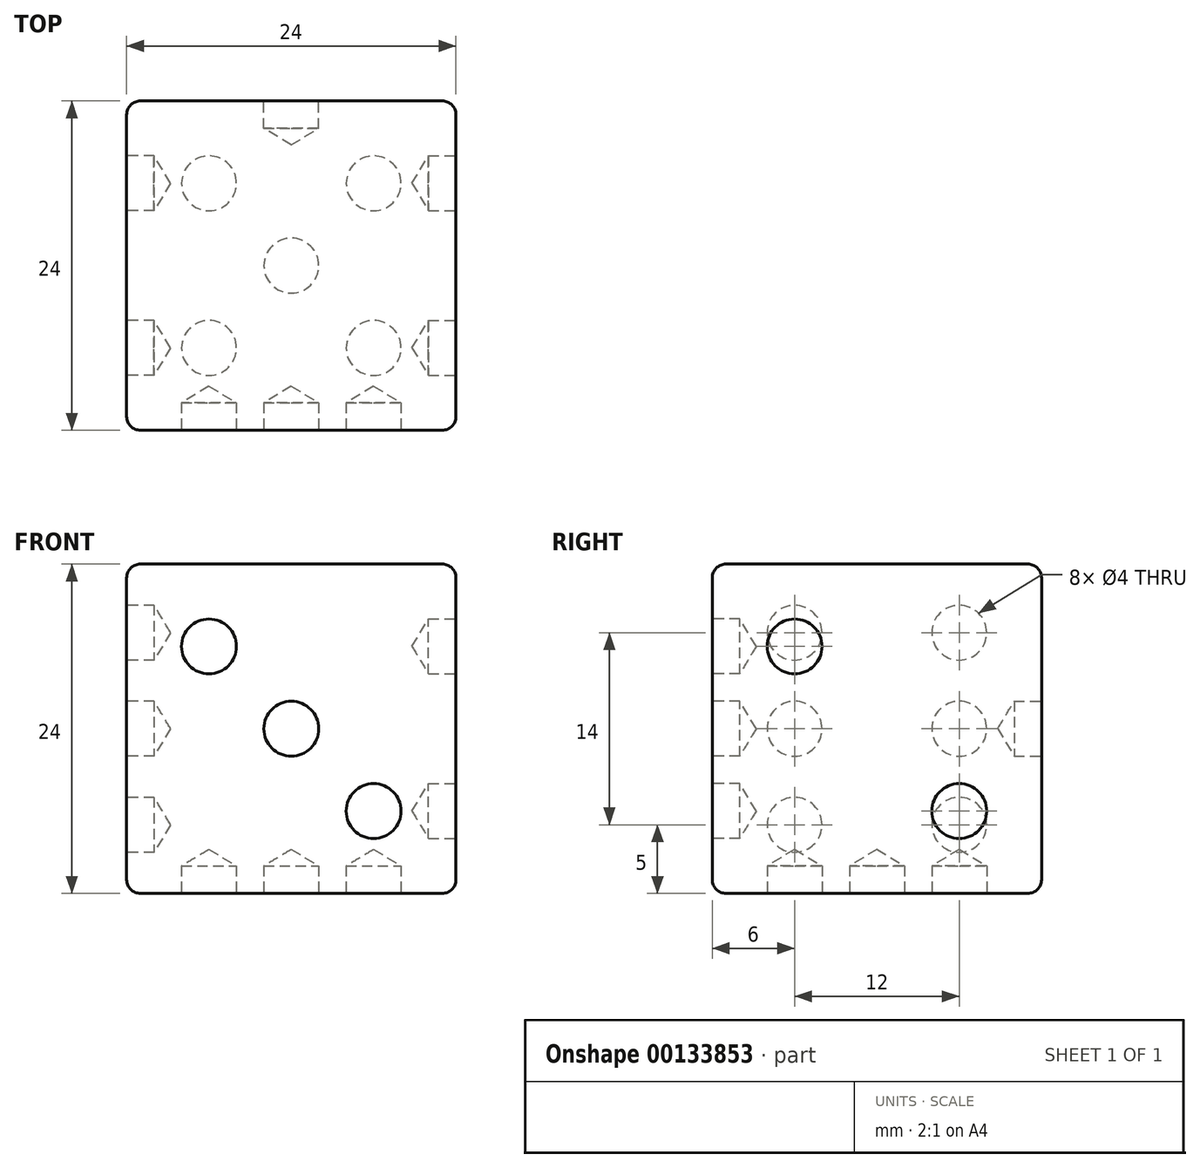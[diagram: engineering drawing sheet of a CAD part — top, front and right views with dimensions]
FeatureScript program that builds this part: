
annotation { "Feature Type Name" : "Feature", "Feature Type Description" : "" }
export const myFeature = defineFeature(function(context is Context, id is Id, definition is map)
    precondition{}
    {
        {
            var Q0;
            Q0=qCreatedBy(makeId("Top.planeOp"),FACE);
            var sketch = newSketch(context, id + "F0", { "sketchPlane" : qUnion([Q0])});
            skLineSegment(sketch, "E0.bottom", {"start": v(12, -12) * mm, "end": v(-12, -12) * mm});
            skLineSegment(sketch, "E0.top", {"start": v(12, 12) * mm, "end": v(-12, 12) * mm});
            skLineSegment(sketch, "E0.left", {"start": v(12, -12) * mm, "end": v(12, 12) * mm});
            skLineSegment(sketch, "E0.right", {"start": v(-12, -12) * mm, "end": v(-12, 12) * mm});
            skPoint(sketch, "E0.middle", {"position": v(0, 0) * mm});
            skCircle(sketch, "E1", {"center": v(-6, 6) * mm, "radius": 2 * mm});
            skCircle(sketch, "E2.0.1.0", {"center": v(-6, -6) * mm, "radius": 2 * mm});
            skCircle(sketch, "E2.1.0.0", {"center": v(6, 6) * mm, "radius": 2 * mm});
            skCircle(sketch, "E2.1.1.0", {"center": v(6, -6) * mm, "radius": 2 * mm});
            skLineSegment(sketch, "E2.direction1", {"start": v(-6.5, 6.5) * mm, "end": v(5.5, 6.5) * mm, "construction": true});
            skLineSegment(sketch, "E2.direction2", {"start": v(-6.5, 6.5) * mm, "end": v(-6.5, -5.5) * mm, "construction": true});
            skCircle(sketch, "E3", {"center": v(0, 0) * mm, "radius": 2 * mm});
            skSolve(sketch);
        }
        {
            var Q0;
            Q0=makeQuery(id+"F0.imprint","IMPRINT",FACE,{"disambiguationData":[TD([[makeQuery(id+"F0.imprint","IMPRINT",EDGE,{"derivedFrom":sQuery(id+"F0.wireOp",EDGE,"E0.bottom")}),-1.0]])]});
            var Q1;
            Q1=makeQuery(id+"F0.imprint","IMPRINT",FACE,{"disambiguationData":[TD([[makeQuery(id+"F0.imprint","IMPRINT",EDGE,{"derivedFrom":sQuery(id+"F0.wireOp",EDGE,"E2.1.0.0")}),1.0]])]});
            var Q2;
            Q2=makeQuery(id+"F0.imprint","IMPRINT",FACE,{"disambiguationData":[TD([[makeQuery(id+"F0.imprint","IMPRINT",EDGE,{"derivedFrom":sQuery(id+"F0.wireOp",EDGE,"E1")}),1.0]])]});
            var Q3;
            Q3=makeQuery(id+"F0.imprint","IMPRINT",FACE,{"disambiguationData":[TD([[makeQuery(id+"F0.imprint","IMPRINT",EDGE,{"derivedFrom":sQuery(id+"F0.wireOp",EDGE,"E3")}),1.0]])]});
            var Q4;
            Q4=makeQuery(id+"F0.imprint","IMPRINT",FACE,{"disambiguationData":[TD([[makeQuery(id+"F0.imprint","IMPRINT",EDGE,{"derivedFrom":sQuery(id+"F0.wireOp",EDGE,"E2.0.1.0")}),1.0]])]});
            var Q5;
            Q5=makeQuery(id+"F0.imprint","IMPRINT",FACE,{"disambiguationData":[TD([[makeQuery(id+"F0.imprint","IMPRINT",EDGE,{"derivedFrom":sQuery(id+"F0.wireOp",EDGE,"E2.1.1.0")}),1.0]])]});
            extrude(context, id + "F1", {"entities" : qUnion([Q0, Q1, Q2, Q3, Q4, Q5]), "depth" : 24 * mm});
        }
        {
            var Q0;
            Q0=makeQuery(id+"F1.opExtrude","SWEPT_FACE",FACE,{"disambiguationData":[OSD([sQuery(id+"F0.wireOp",EDGE,"E0.bottom")])]});
            var sketch = newSketch(context, id + "F2", { "sketchPlane" : qUnion([Q0])});
            skCircle(sketch, "E4", {"center": v(-6, 18) * mm, "radius": 2 * mm});
            skCircle(sketch, "E5", {"center": v(0, 12) * mm, "radius": 2 * mm});
            skCircle(sketch, "E6", {"center": v(6, 6) * mm, "radius": 2 * mm});
            skSolve(sketch);
        }
        {
            var Q0;
            Q0=makeQuery(id+"F1.opExtrude","SWEPT_FACE",FACE,{"disambiguationData":[OSD([sQuery(id+"F0.wireOp",EDGE,"E0.right")])]});
            var sketch = newSketch(context, id + "F3", { "sketchPlane" : qUnion([Q0])});
            skCircle(sketch, "E7", {"center": v(-6, 19) * mm, "radius": 2 * mm});
            skCircle(sketch, "E8.0.1.0", {"center": v(-6, 12) * mm, "radius": 2 * mm});
            skCircle(sketch, "E8.0.2.0", {"center": v(-6, 5) * mm, "radius": 2 * mm});
            skCircle(sketch, "E8.1.0.0", {"center": v(6, 19) * mm, "radius": 2 * mm});
            skCircle(sketch, "E8.1.1.0", {"center": v(6, 12) * mm, "radius": 2 * mm});
            skCircle(sketch, "E8.1.2.0", {"center": v(6, 5) * mm, "radius": 2 * mm});
            skLineSegment(sketch, "E8.direction1", {"start": v(-6, 19) * mm, "end": v(6, 19) * mm, "construction": true});
            skLineSegment(sketch, "E8.direction2", {"start": v(-6, 19) * mm, "end": v(-6, 12) * mm, "construction": true});
            skSolve(sketch);
        }
        {
            var Q0;
            Q0=makeQuery(id+"F1.opExtrude","SWEPT_FACE",FACE,{"disambiguationData":[OSD([sQuery(id+"F0.wireOp",EDGE,"E0.left")])]});
            var sketch = newSketch(context, id + "F4", { "sketchPlane" : qUnion([Q0])});
            skCircle(sketch, "E9", {"center": v(-6, 18) * mm, "radius": 2 * mm});
            skCircle(sketch, "E10", {"center": v(6, 6) * mm, "radius": 2 * mm});
            skSolve(sketch);
        }
        {
            var Q0;
            Q0=makeQuery(id+"F1.opExtrude","SWEPT_FACE",FACE,{"disambiguationData":[OSD([sQuery(id+"F0.wireOp",EDGE,"E0.top")])]});
            var sketch = newSketch(context, id + "F5", { "sketchPlane" : qUnion([Q0])});
            skCircle(sketch, "E11", {"center": v(0, 12) * mm, "radius": 2 * mm});
            skSolve(sketch);
        }
        {
            var Q0;
            Q0=sQuery(id+"F2.wireOp",VERTEX,"E4.center");
            var Q1;
            Q1=sQuery(id+"F2.wireOp",VERTEX,"E5.center");
            var Q2;
            Q2=sQuery(id+"F2.wireOp",VERTEX,"E6.center");
            var Q3;
            Q3=makeQuery(id+"F1.opExtrude","SWEPT_BODY",BODY,{"disambiguationData":[OSD([sQuery(id+"F0.wireOp",EDGE,"E0.bottom"),sQuery(id+"F0.wireOp",EDGE,"E0.top"),sQuery(id+"F0.wireOp",EDGE,"E0.left"),sQuery(id+"F0.wireOp",EDGE,"E0.right")])]});
            hole(context, id + "F6", {"style" : HoleStyle.SIMPLE, "endStyle" : HoleEndStyle.BLIND, "holeDiameter" : 4 * mm, "holeDepth" : 2 * mm, "locations" : qUnion([Q0, Q1, Q2]), "scope" : qUnion([Q3])});
        }
        {
            var Q0;
            Q0=sQuery(id+"F3.wireOp",VERTEX,"E8.1.0.0.center");
            var Q1;
            Q1=sQuery(id+"F3.wireOp",VERTEX,"E8.1.1.0.center");
            var Q2;
            Q2=sQuery(id+"F3.wireOp",VERTEX,"E8.1.2.0.center");
            var Q3;
            Q3=sQuery(id+"F3.wireOp",VERTEX,"E7.center");
            var Q4;
            Q4=sQuery(id+"F3.wireOp",VERTEX,"E8.0.1.0.center");
            var Q5;
            Q5=sQuery(id+"F3.wireOp",VERTEX,"E8.0.2.0.center");
            var Q6;
            Q6=makeQuery(id+"F1.opExtrude","SWEPT_BODY",BODY,{"disambiguationData":[OSD([sQuery(id+"F0.wireOp",EDGE,"E0.bottom"),sQuery(id+"F0.wireOp",EDGE,"E0.top"),sQuery(id+"F0.wireOp",EDGE,"E0.left"),sQuery(id+"F0.wireOp",EDGE,"E0.right")])]});
            hole(context, id + "F7", {"style" : HoleStyle.SIMPLE, "endStyle" : HoleEndStyle.BLIND, "holeDiameter" : 4 * mm, "holeDepth" : 2 * mm, "locations" : qUnion([Q0, Q1, Q2, Q3, Q4, Q5]), "scope" : qUnion([Q6])});
        }
        {
            var Q0;
            Q0=sQuery(id+"F0.wireOp",VERTEX,"E2.0.1.0.center");
            var Q1;
            Q1=sQuery(id+"F0.wireOp",VERTEX,"E2.1.1.0.center");
            var Q2;
            Q2=sQuery(id+"F0.wireOp",VERTEX,"E1.center");
            var Q3;
            Q3=sQuery(id+"F0.wireOp",VERTEX,"E2.1.0.0.center");
            var Q4;
            Q4=sQuery(id+"F0.wireOp",VERTEX,"E0.middle");
            var Q5;
            Q5=makeQuery(id+"F1.opExtrude","SWEPT_BODY",BODY,{"disambiguationData":[OSD([sQuery(id+"F0.wireOp",EDGE,"E0.bottom"),sQuery(id+"F0.wireOp",EDGE,"E0.top"),sQuery(id+"F0.wireOp",EDGE,"E0.left"),sQuery(id+"F0.wireOp",EDGE,"E0.right")])]});
            hole(context, id + "F8", {"style" : HoleStyle.SIMPLE, "endStyle" : HoleEndStyle.BLIND, "oppositeDirection" : true, "holeDiameter" : 4 * mm, "holeDepth" : 2 * mm, "locations" : qUnion([Q0, Q1, Q2, Q3, Q4]), "scope" : qUnion([Q5])});
        }
        {
            var Q0;
            Q0=sQuery(id+"F4.wireOp",VERTEX,"E9.center");
            var Q1;
            Q1=sQuery(id+"F4.wireOp",VERTEX,"E10.center");
            var Q2;
            Q2=sQuery(id+"F5.wireOp",VERTEX,"E11.center");
            var Q3;
            Q3=makeQuery(id+"F1.opExtrude","SWEPT_BODY",BODY,{"disambiguationData":[OSD([sQuery(id+"F0.wireOp",EDGE,"E0.bottom"),sQuery(id+"F0.wireOp",EDGE,"E0.top"),sQuery(id+"F0.wireOp",EDGE,"E0.left"),sQuery(id+"F0.wireOp",EDGE,"E0.right")])]});
            hole(context, id + "F9", {"style" : HoleStyle.SIMPLE, "endStyle" : HoleEndStyle.BLIND, "holeDiameter" : 4 * mm, "holeDepth" : 2 * mm, "locations" : qUnion([Q0, Q1, Q2]), "scope" : qUnion([Q3])});
        }
        {
            var Q0;
            Q0=makeQuery(id+"F1.opExtrude","CAP_EDGE",EDGE,{"disambiguationData":[OSD([sQuery(id+"F0.wireOp",EDGE,"E0.bottom")])],"isStart":true});
            var Q1;
            Q1=makeQuery(id+"F1.opExtrude","CAP_EDGE",EDGE,{"disambiguationData":[OSD([sQuery(id+"F0.wireOp",EDGE,"E0.right")])],"isStart":true});
            var Q2;
            Q2=makeQuery(id+"F1.opExtrude","SWEPT_EDGE",EDGE,{"disambiguationData":[OSD([sQuery(id+"F0.wireOp",EDGE,"E0.bottom"),sQuery(id+"F0.wireOp",EDGE,"E0.right")])]});
            var Q3;
            Q3=makeQuery(id+"F1.opExtrude","CAP_EDGE",EDGE,{"disambiguationData":[OSD([sQuery(id+"F0.wireOp",EDGE,"E0.left")])],"isStart":true});
            var Q4;
            Q4=makeQuery(id+"F1.opExtrude","CAP_EDGE",EDGE,{"disambiguationData":[OSD([sQuery(id+"F0.wireOp",EDGE,"E0.top")])],"isStart":true});
            var Q5;
            Q5=makeQuery(id+"F1.opExtrude","SWEPT_EDGE",EDGE,{"disambiguationData":[OSD([sQuery(id+"F0.wireOp",EDGE,"E0.bottom"),sQuery(id+"F0.wireOp",EDGE,"E0.left")])]});
            var Q6;
            Q6=makeQuery(id+"F1.opExtrude","CAP_EDGE",EDGE,{"disambiguationData":[OSD([sQuery(id+"F0.wireOp",EDGE,"E0.bottom")])],"isStart":false});
            var Q7;
            Q7=makeQuery(id+"F1.opExtrude","CAP_EDGE",EDGE,{"disambiguationData":[OSD([sQuery(id+"F0.wireOp",EDGE,"E0.right")])],"isStart":false});
            var Q8;
            Q8=makeQuery(id+"F1.opExtrude","SWEPT_EDGE",EDGE,{"disambiguationData":[OSD([sQuery(id+"F0.wireOp",EDGE,"E0.top"),sQuery(id+"F0.wireOp",EDGE,"E0.right")])]});
            var Q9;
            Q9=makeQuery(id+"F1.opExtrude","CAP_EDGE",EDGE,{"disambiguationData":[OSD([sQuery(id+"F0.wireOp",EDGE,"E0.top")])],"isStart":false});
            var Q10;
            Q10=makeQuery(id+"F1.opExtrude","SWEPT_EDGE",EDGE,{"disambiguationData":[OSD([sQuery(id+"F0.wireOp",EDGE,"E0.top"),sQuery(id+"F0.wireOp",EDGE,"E0.left")])]});
            var Q11;
            Q11=makeQuery(id+"F1.opExtrude","CAP_EDGE",EDGE,{"disambiguationData":[OSD([sQuery(id+"F0.wireOp",EDGE,"E0.left")])],"isStart":false});
            fillet(context, id + "F10", {"entities" : qUnion([Q0, Q1, Q2, Q3, Q4, Q5, Q6, Q7, Q8, Q9, Q10, Q11]), "radius" : 1 * mm, "allowEdgeOverflow" : false});
        }
    });
